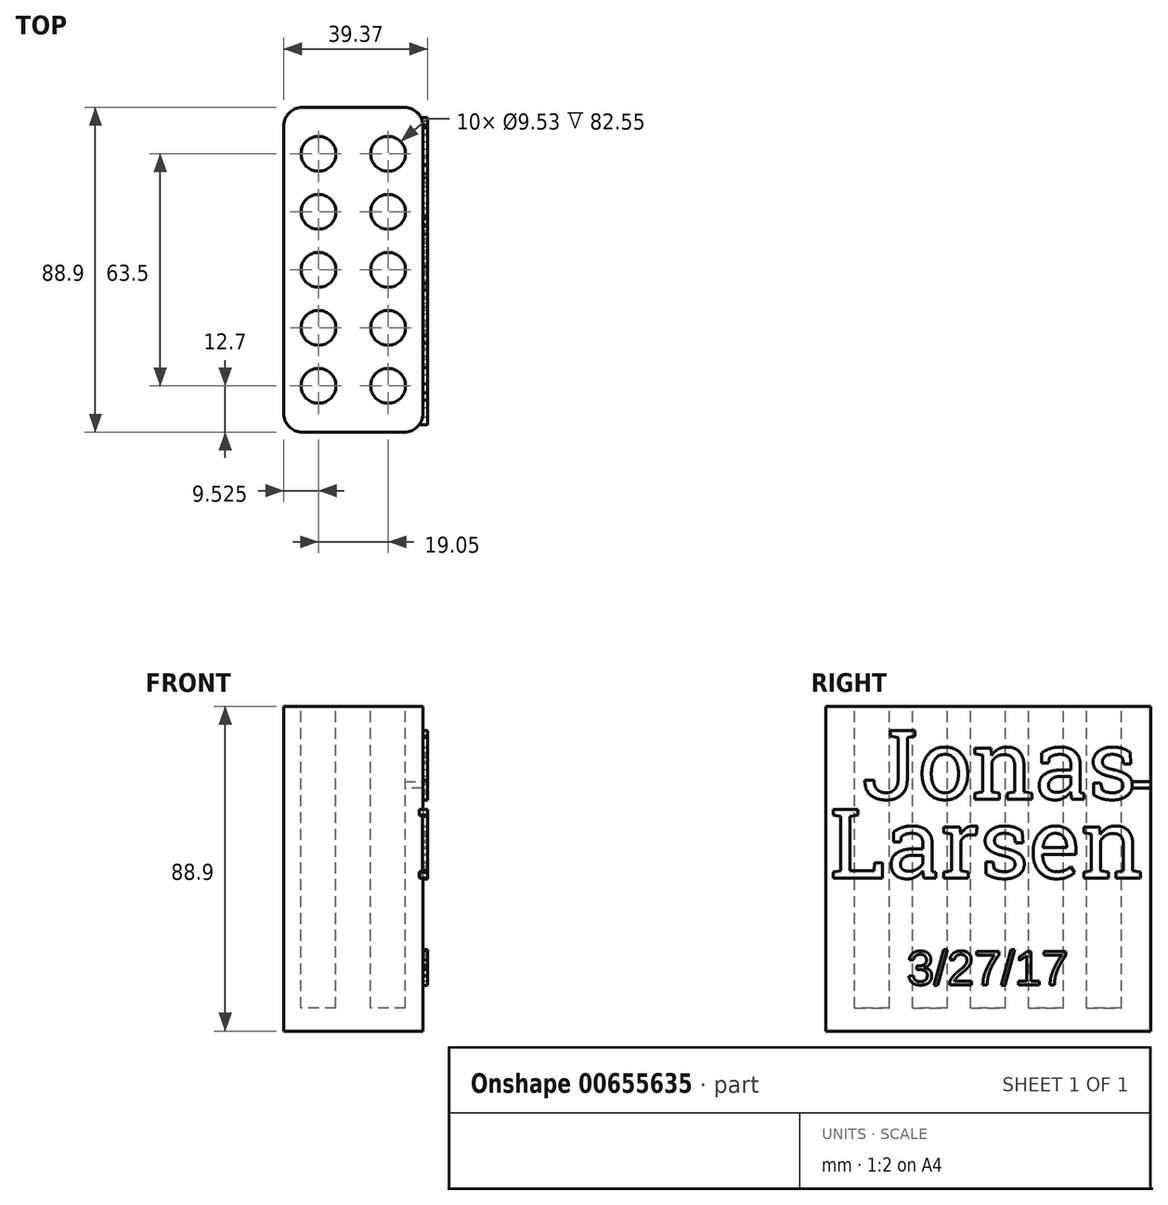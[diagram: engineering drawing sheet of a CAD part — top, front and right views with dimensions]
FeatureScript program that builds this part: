
annotation { "Feature Type Name" : "Feature", "Feature Type Description" : "" }
export const myFeature = defineFeature(function(context is Context, id is Id, definition is map)
    precondition{}
    {
        {
            var Q0;
            Q0=qCreatedBy(makeId("Right.planeOp"),FACE);
            var sketch = newSketch(context, id + "F0", { "sketchPlane" : qUnion([Q0])});
            skLineSegment(sketch, "E0.bottom", {"start": v(-44.45, 44.45) * mm, "end": v(44.45, 44.45) * mm});
            skLineSegment(sketch, "E0.top", {"start": v(-44.45, -44.45) * mm, "end": v(44.45, -44.45) * mm});
            skLineSegment(sketch, "E0.left", {"start": v(-44.45, 44.45) * mm, "end": v(-44.45, -44.45) * mm});
            skLineSegment(sketch, "E0.right", {"start": v(44.45, 44.45) * mm, "end": v(44.45, -44.45) * mm});
            skPoint(sketch, "E0.middle", {"position": v(0, 0) * mm});
            skSolve(sketch);
        }
        {
            var Q0;
            Q0 = qSketchRegion(id + "F0", true);
            extrude(context, id + "F1", {"entities" : qUnion([Q0]), "endBound" : BoundingType.SYMMETRIC, "depth" : 38.1 * mm, "offsetDistance" : 25.4 * mm});
        }
        {
            var Q0;
            Q0=makeQuery(id+"F1.opExtrude","SWEPT_FACE",FACE,{"disambiguationData":[OSD([sQuery(id+"F0.wireOp",EDGE,"E0.bottom")])]});
            var sketch = newSketch(context, id + "F2", { "sketchPlane" : qUnion([Q0])});
            skCircle(sketch, "E1", {"center": v(-9.52, -31.75) * mm, "radius": 4.76 * mm});
            skCircle(sketch, "E2", {"center": v(-9.52, 0) * mm, "radius": 4.76 * mm});
            skCircle(sketch, "E3", {"center": v(-9.52, -15.88) * mm, "radius": 4.76 * mm});
            skCircle(sketch, "E4", {"center": v(-9.52, 15.88) * mm, "radius": 4.76 * mm});
            skCircle(sketch, "E5", {"center": v(-9.52, 31.75) * mm, "radius": 4.76 * mm});
            skCircle(sketch, "E6.MirrorC", {"center": v(9.52, 0) * mm, "radius": 4.76 * mm});
            skCircle(sketch, "E7.MirrorC", {"center": v(9.52, -31.75) * mm, "radius": 4.76 * mm});
            skCircle(sketch, "E8.MirrorC", {"center": v(9.52, -15.88) * mm, "radius": 4.76 * mm});
            skCircle(sketch, "E9.MirrorC", {"center": v(9.52, 15.88) * mm, "radius": 4.76 * mm});
            skCircle(sketch, "E10.MirrorC", {"center": v(9.52, 31.75) * mm, "radius": 4.76 * mm});
            skSolve(sketch);
        }
        {
            var Q0;
            Q0 = qSketchRegion(id + "F2", true);
            extrude(context, id + "F3", {"entities" : qUnion([Q0]), "operationType" : NewBodyOperationType.REMOVE, "oppositeDirection" : true, "depth" : 82.55 * mm, "offsetDistance" : 25.4 * mm});
        }
        {
            var Q0;
            Q0=makeQuery(id+"F1.opExtrude","CAP_FACE",FACE,{"disambiguationData":[OSD([sQuery(id+"F0.wireOp",EDGE,"E0.bottom"),sQuery(id+"F0.wireOp",EDGE,"E0.top"),sQuery(id+"F0.wireOp",EDGE,"E0.left"),sQuery(id+"F0.wireOp",EDGE,"E0.right")])],"isStart":false});
            var sketch = newSketch(context, id + "F4", { "sketchPlane" : qUnion([Q0])});
            skText(sketch, "E11", { "text": " Jonas", "fontName": "RobotoSlab-Regular.ttf"});
            skText(sketch, "E12", { "text": "3/27/17", "fontName": "Arimo-Regular.ttf"});
            skText(sketch, "E13", { "text": "Larsen", "fontName": "RobotoSlab-Regular.ttf"});
            const initialGuessF4  = {"E11": [-0.0411, 0.01905, 1, 0, 0.01905], "E12": [-0.0222, -0.03175, 1, 0, 0.00953], "E13": [-0.04335, -0.00254, 1, 0, 0.01905]};
            skSetInitialGuess(sketch, initialGuessF4);
            skSolve(sketch);
        }
        {
            var Q0;
            Q0 = qSketchRegion(id + "F4", true);
            extrude(context, id + "F5", {"entities" : qUnion([Q0]), "operationType" : NewBodyOperationType.ADD, "depth" : 1.27 * mm, "offsetDistance" : 25.4 * mm});
        }
        {
            var Q0;
            Q0=makeQuery(id+"F1.opExtrude","CAP_EDGE",EDGE,{"disambiguationData":[OSD([sQuery(id+"F0.wireOp",EDGE,"E0.left")])],"isStart":false});
            var Q1;
            Q1=makeQuery(id+"F1.opExtrude","CAP_EDGE",EDGE,{"disambiguationData":[OSD([sQuery(id+"F0.wireOp",EDGE,"E0.right")])],"isStart":false});
            var Q2;
            Q2=makeQuery(id+"F1.opExtrude","CAP_EDGE",EDGE,{"disambiguationData":[OSD([sQuery(id+"F0.wireOp",EDGE,"E0.right")])],"isStart":true});
            var Q3;
            Q3=makeQuery(id+"F1.opExtrude","CAP_EDGE",EDGE,{"disambiguationData":[OSD([sQuery(id+"F0.wireOp",EDGE,"E0.left")])],"isStart":true});
            fillet(context, id + "F6", {"entities" : qUnion([Q0, Q1, Q2, Q3]), "radius" : 5.08 * mm, "tangentPropagation" : true, "allowEdgeOverflow" : false});
        }
    });
